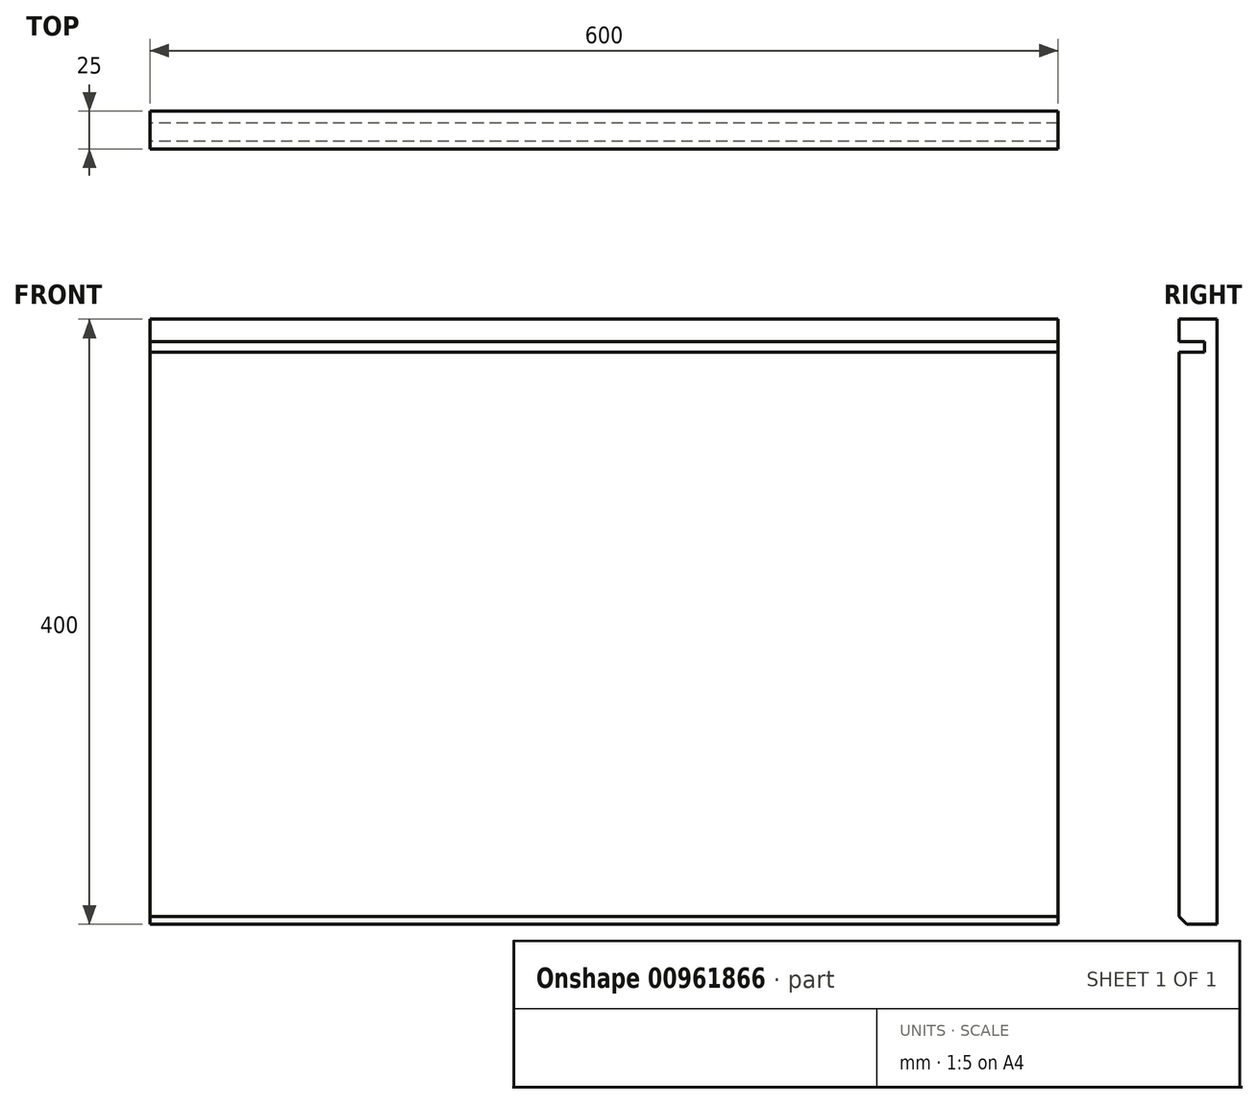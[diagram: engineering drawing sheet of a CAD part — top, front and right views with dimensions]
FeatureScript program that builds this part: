
annotation { "Feature Type Name" : "Feature", "Feature Type Description" : "" }
export const myFeature = defineFeature(function(context is Context, id is Id, definition is map)
    precondition{}
    {
        {
            var Q0;
            Q0=qCreatedBy(makeId("Front.planeOp"),FACE);
            var sketch = newSketch(context, id + "F0", { "sketchPlane" : qUnion([Q0])});
            skLineSegment(sketch, "E0.bottom", {"start": v(-15221.78, 382.37) * mm, "end": v(-14621.78, 382.37) * mm});
            skLineSegment(sketch, "E0.top", {"start": v(-15221.78, -17.63) * mm, "end": v(-14621.78, -17.63) * mm});
            skLineSegment(sketch, "E0.left", {"start": v(-15221.78, 382.37) * mm, "end": v(-15221.78, -17.63) * mm});
            skLineSegment(sketch, "E0.right", {"start": v(-14621.78, 382.37) * mm, "end": v(-14621.78, -17.63) * mm});
            skSolve(sketch);
        }
        {
            var Q0;
            Q0 = qSketchRegion(id + "F0", true);
            extrude(context, id + "F1", {"entities" : qUnion([Q0]), "depth" : 25 * mm, "offsetDistance" : 25 * mm});
        }
        {
            var Q0;
            Q0=makeQuery(id+"F1.opExtrude","CAP_EDGE",EDGE,{"disambiguationData":[OSD([sQuery(id+"F0.wireOp",EDGE,"E0.top")])],"isStart":false});
            chamfer(context, id + "F2", {"entities" : qUnion([Q0]), "width" : 5 * mm, "tangentPropagation" : true});
        }
        {
            var Q0;
            Q0=makeQuery(id+"F1.opExtrude","SWEPT_FACE",FACE,{"disambiguationData":[OSD([sQuery(id+"F0.wireOp",EDGE,"E0.left")])]});
            var sketch = newSketch(context, id + "F3", { "sketchPlane" : qUnion([Q0])});
            skLineSegment(sketch, "E1.bottom", {"start": v(44.97, 367.37) * mm, "end": v(8, 367.37) * mm});
            skLineSegment(sketch, "E1.top", {"start": v(44.97, 360.37) * mm, "end": v(8, 360.37) * mm});
            skLineSegment(sketch, "E1.left", {"start": v(44.97, 367.37) * mm, "end": v(44.97, 360.37) * mm});
            skLineSegment(sketch, "E1.right", {"start": v(8, 367.37) * mm, "end": v(8, 360.37) * mm});
            skSolve(sketch);
        }
        {
            var Q0;
            Q0 = qSketchRegion(id + "F3", true);
            extrude(context, id + "F4", {"entities" : qUnion([Q0]), "operationType" : NewBodyOperationType.REMOVE, "oppositeDirection" : true, "depth" : 1000 * mm, "offsetDistance" : 25 * mm});
        }
    });
